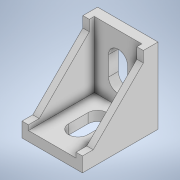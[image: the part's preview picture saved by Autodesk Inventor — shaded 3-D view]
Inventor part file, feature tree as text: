
AUTODESK INVENTOR PART (.ipt)
format: ipt  version: 2022 (Build 260153000, 153)  size: 180,736 bytes
history: native  units: mm
features: extrude x6, sketch x6, projected_geometry x6
ambient origin geometry x8: Origin, YZ Plane, XZ Plane, XY Plane, X Axis, Y Axis, Z Axis, Center Point
bodies: Solid1 (feature_tree)
feature tree (18):
  extrude  "Extrusion1"  Depth=28.0mm
  extrude  "Extrusion2"  Depth=17.5mm
  extrude  "Extrusion3"  Depth=6.8mm
  extrude  "Extrusion4"  Depth=3.0mm TaperAngle=0.0deg
  extrude  "Extrusion5"  Depth=4.5mm TaperAngle=0.0deg
  extrude  "Extrusion6"  Depth=10.0mm
  sketch  "Sketch1"  dims[d0=35.0mm d1=28.0mm]
  sketch  "Sketch2"  dims[d2=14.0mm d3=17.5mm]
  projected_geometry  "Projected Loop1"
  sketch  "Sketch3"  dims[d4=4.5mm d5=0.0mm d6=6.8mm]
  projected_geometry  "Projected Loop2"
  projected_geometry  "Projected Loop3"
  sketch  "Sketch4"  dims[d7=5.0mm d8=3.0mm d9=0.0mm]
  projected_geometry  "Projected Loop4"
  sketch  "Sketch5"  dims[d10=3.0mm d11=0.0mm d12=4.5mm d13=0.0mm]
  projected_geometry  "Projected Loop5"
  projected_geometry  "Projected Loop6"
  sketch  "Sketch6"  dims[d14=14.0mm d15=9.0mm d16=8.8mm d17=4.5mm d18=0.0mm d19=9.0mm d20=8.8mm d21=14.0mm d22=14.0mm d23=10.0mm d24=0.0mm]
